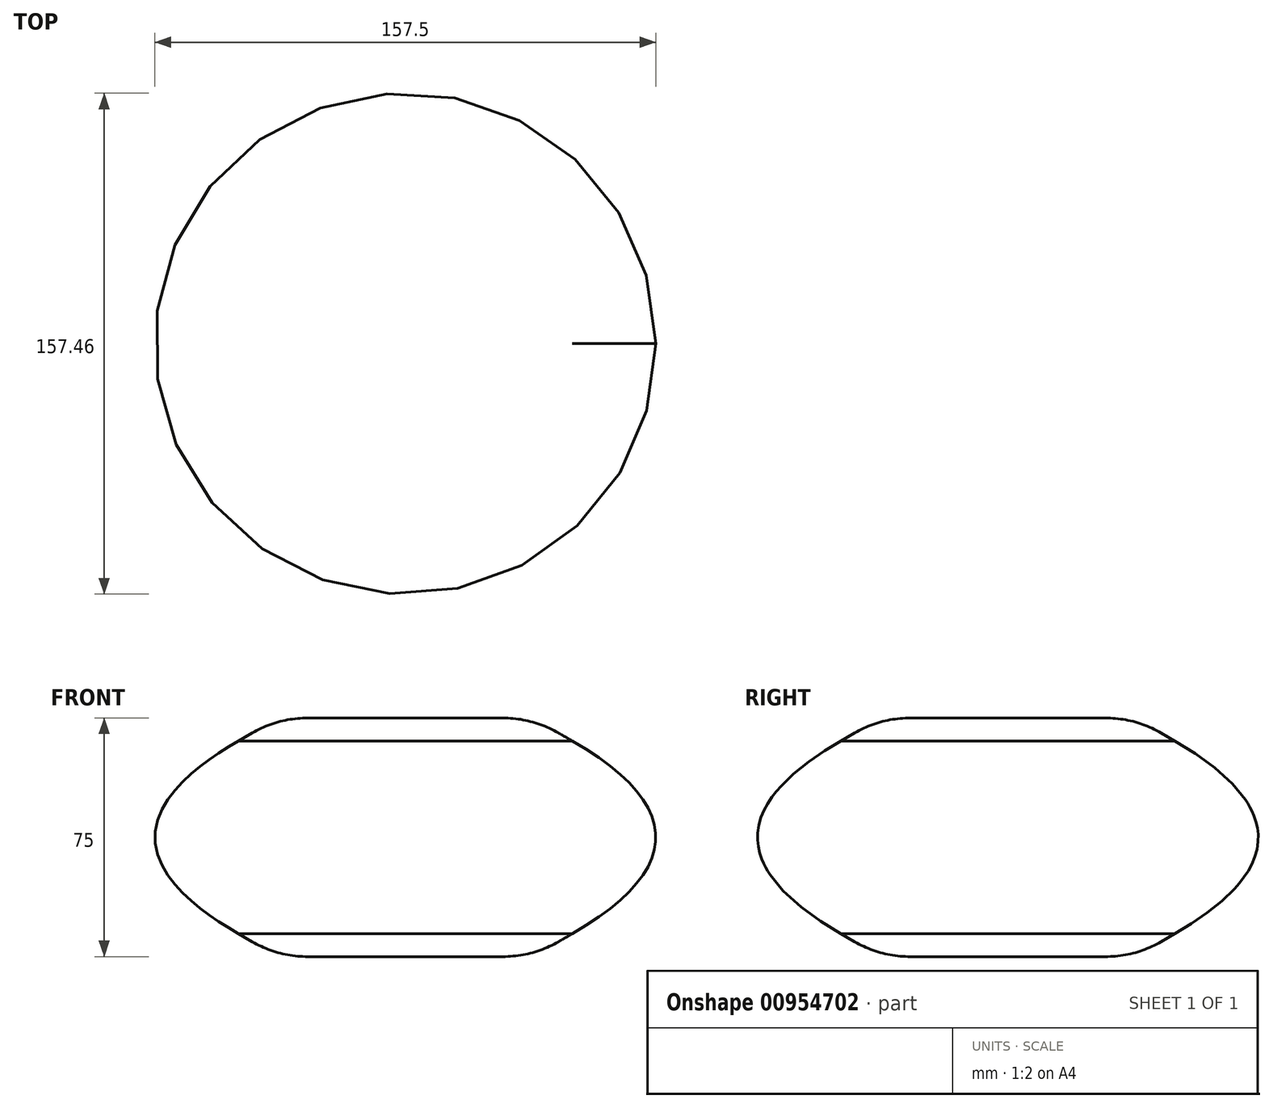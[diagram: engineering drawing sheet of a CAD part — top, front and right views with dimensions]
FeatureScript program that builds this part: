
annotation { "Feature Type Name" : "Feature", "Feature Type Description" : "" }
export const myFeature = defineFeature(function(context is Context, id is Id, definition is map)
    precondition{}
    {
        {
            var Q0;
            Q0=qCreatedBy(makeId("Top.planeOp"),FACE);
            var sketch = newSketch(context, id + "F0", { "sketchPlane" : qUnion([Q0])});
            skCircle(sketch, "E0", {"center": v(0, 0) * mm, "radius": 105 * mm});
            skSolve(sketch);
        }
        {
            var Q0;
            Q0 = qSketchRegion(id + "F0", true);
            var Q1;
            Q1=sQuery(id+"F0.wireOp",EDGE,"E0");
            extrude(context, id + "F1", {"entities" : qUnion([Q0]), "surfaceEntities" : qUnion([Q1]), "endBound" : BoundingType.SYMMETRIC, "depth" : 75 * mm, "offsetDistance" : 25 * mm, "hasDraft" : true, "draftAngle" : 60 * degree, "draftPullDirection" : true});
        }
        {
            var Q0;
            Q0=makeQuery(id+"F1.opExtrude","CAP_FACE",FACE,{"disambiguationData":[OSD([sQuery(id+"F0.wireOp",EDGE,"E0")])],"isStart":false});
            var sketch = newSketch(context, id + "F2", { "sketchPlane" : qUnion([Q0])});
            skCircle(sketch, "E1", {"center": v(0, 0) * mm, "radius": 10 * mm});
            skSolve(sketch);
        }
        {
            var Q0;
            Q0 = qSketchRegion(id + "F2", true);
            var Q1;
            Q1=sQuery(id+"F2.wireOp",EDGE,"E1");
            extrude(context, id + "F3", {"entities" : qUnion([Q0]), "bodyType" : ToolBodyType.SURFACE, "surfaceEntities" : qUnion([Q1]), "depth" : 300 * mm, "offsetDistance" : 25 * mm});
        }
        {
            var Q0;
            Q0=makeQuery(id+"F1.opExtrude","CAP_FACE",FACE,{"disambiguationData":[OSD([sQuery(id+"F0.wireOp",EDGE,"E0")])],"isStart":false});
            var sketch = newSketch(context, id + "F4", { "sketchPlane" : qUnion([Q0])});
            skCircle(sketch, "E2", {"center": v(-30, 0) * mm, "radius": 5 * mm});
            skSolve(sketch);
        }
        {
            var Q0;
            Q0=sQuery(id+"F4.wireOp",EDGE,"E2");
            extrude(context, id + "F5", {"bodyType" : ToolBodyType.SURFACE, "surfaceEntities" : qUnion([Q0]), "oppositeDirection" : true, "depth" : 73 * mm, "offsetDistance" : 25 * mm});
        }
        {
            var Q0;
            Q0=makeQuery(id+"F1.*.split.splitOp","SPLIT",FACE,{"derivedFrom":makeQuery(id+"F1.opExtrude","SWEPT_FACE",FACE,{"disambiguationData":[OSD([sQuery(id+"F0.wireOp",EDGE,"E0")])]}),"isFromBackBody":true});
            var Q1;
            Q1=makeQuery(id+"F1.*.split.splitOp","SPLIT",FACE,{"derivedFrom":makeQuery(id+"F1.opExtrude","SWEPT_FACE",FACE,{"disambiguationData":[OSD([sQuery(id+"F0.wireOp",EDGE,"E0")])]})});
            fillet(context, id + "F6", {"entities" : qUnion([Q0, Q1]), "radius" : 35 * mm, "tangentPropagation" : true, "rho" : 0.5, "crossSection" : FilletCrossSection.CONIC, "allowEdgeOverflow" : false});
        }
    });
